# Revit family: Window_Curtain_Wall-Project_Out-Traco-NX_3500-Heavy_Commercial
name_source: partatom
category: Windows
revit_build: Autodesk Revit 2015 (Build: 20140905_0730(x64)
units: mm (PartAtom-declared; Revit-internal decimal feet)

## types (4) — shared parameters
Allowable Air Infiltration Maximum = 0.1 @ 6.2 PSF
Assembly Code = B2020110
CTRL Panel Active Frame Width = 0' - 2 1/4"
Condensation Resistance = 43.0000 psf
Depth = 0' - 3 1/4"
Description = Overlap Projected Architectural Thermal Aluminum Windows
Designation = AAMA/WDMA/CSA 101/I.S.2/A-440-05: AP-AW80 And AAMA/WDMA/CSA 101/I.S.2/A-440-08: AW-PG80-AP
Forced Entry Resistance = TYPE B: GRADE 10
Frame Material = Aluminum - Traco - Anodized - Bronze
Glazing Material = Glass - Traco - Clear
Glazing Thickness = 0' - 1"
Head Width = 0' - 2 1/4"
Height Maximum = 5' - 0"
Height Minimum = 2' - 0"
Is Dual Glazed = No
Is Triple Glazed = No
Jamb Width = 0' - 2 1/4"
Keynote = 08520
Manufacturer = Traco
Model = NX-3500
Product Documentation Link = http://www.alcoa.com
Product Page URL = http://www.alcoa.com
Product data url = https://bimobject.com
Screen Material = Aluminum - Traco - Screen
Sill Width = 0' - 2 1/4"
Test Size = 60" X 36"
Type Comments = Project Out
U Factor = .42 Per NFRC 100
URL = http://www.alcoa.com
Uniform Load Deflection = 80.0000 psf
Uniform Load Structural = 120.0000 psf
Water Resistance = 15.0000 psf
Width Maximum = 8' - 0"
Width Minimum = 1' - 6"

## per-type parameters (varying)
| type | CTRL Configuration Number | CTRL Mullion Fixed Visibility | Panel Configuration |
| NX-3500 - Project_Out - Single | 1 | No | Vent |
| NX-3500 - Project_Out - Single/Fixed-Top | 3 | Yes | Fixed/Vent-Bottom |
| NX-3500 - Project_Out - Double/Fixed Top | 2 | No | Middle Vent/Middle Vent |
| NX-3500 - Project_Out - Single/Double Fixed-Top | 4 | No | Fixed/Vent-Bottom |

## geometry (parser evidence)
native form markers: Blend x14, Sweep x11
no freeform markers — native parametric forms only
